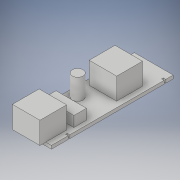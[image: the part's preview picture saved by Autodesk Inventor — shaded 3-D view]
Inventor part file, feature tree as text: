
AUTODESK INVENTOR PART (.ipt)
format: ipt  version: 2018 (Build 220112000, 112)  size: 185,344 bytes
history: native  units: in
note: dims shown in document units (in); Inventor stores cm internally (conversion verified against a paired STEP export)
features: extrude x6, sketch x6
ambient origin geometry x8: Origin, YZ Plane, XZ Plane, XY Plane, X Axis, Y Axis, Z Axis, Center Point
bodies: Solid1 (feature_tree)
feature tree (12):
  extrude  "Extrusion1"  Depth=0.9154in
  extrude  "Extrusion2"  Depth=0.1378in
  extrude  "Extrusion3"  Depth=0.6299in
  extrude  "Extrusion4"  Depth=0.6102in
  extrude  "Extrusion5"  Depth=0.5906in
  extrude  "Extrusion6"  Depth=0.374in
  sketch  "Sketch1"  dims[d0=2.874in d1=0.9154in]
  sketch  "Sketch2"  dims[d2=0.0787in d3=0.0in d4=0.1378in]
  sketch  "Sketch3"  dims[d5=0.6496in d6=0.6299in]
  sketch  "Sketch4"  dims[d7=0.5157in d8=0.0in d9=0.6102in]
  sketch  "Sketch5"  dims[d10=0.6496in d11=0.5906in]
  sketch  "Sketch6"  dims[d12=0.5118in d13=0.0in d14=0.374in d15=0.2362in d16=0.2559in d17=0.4921in d18=0.0in d19=0.2953in d20=0.7169in d21=0.1378in d22=0.2461in d23=0.0in d24=2.2638in d25=0.1969in d26=0.0394in d27=0.0591in d28=0.0in d29=0.0394in d30=0.0591in d31=0.0in d32=0.0in d33=0.0591in d34=0.0394in d35=0.0in d36=0.0591in d37=0.0394in d38=0.2461in d39=0.0in]
